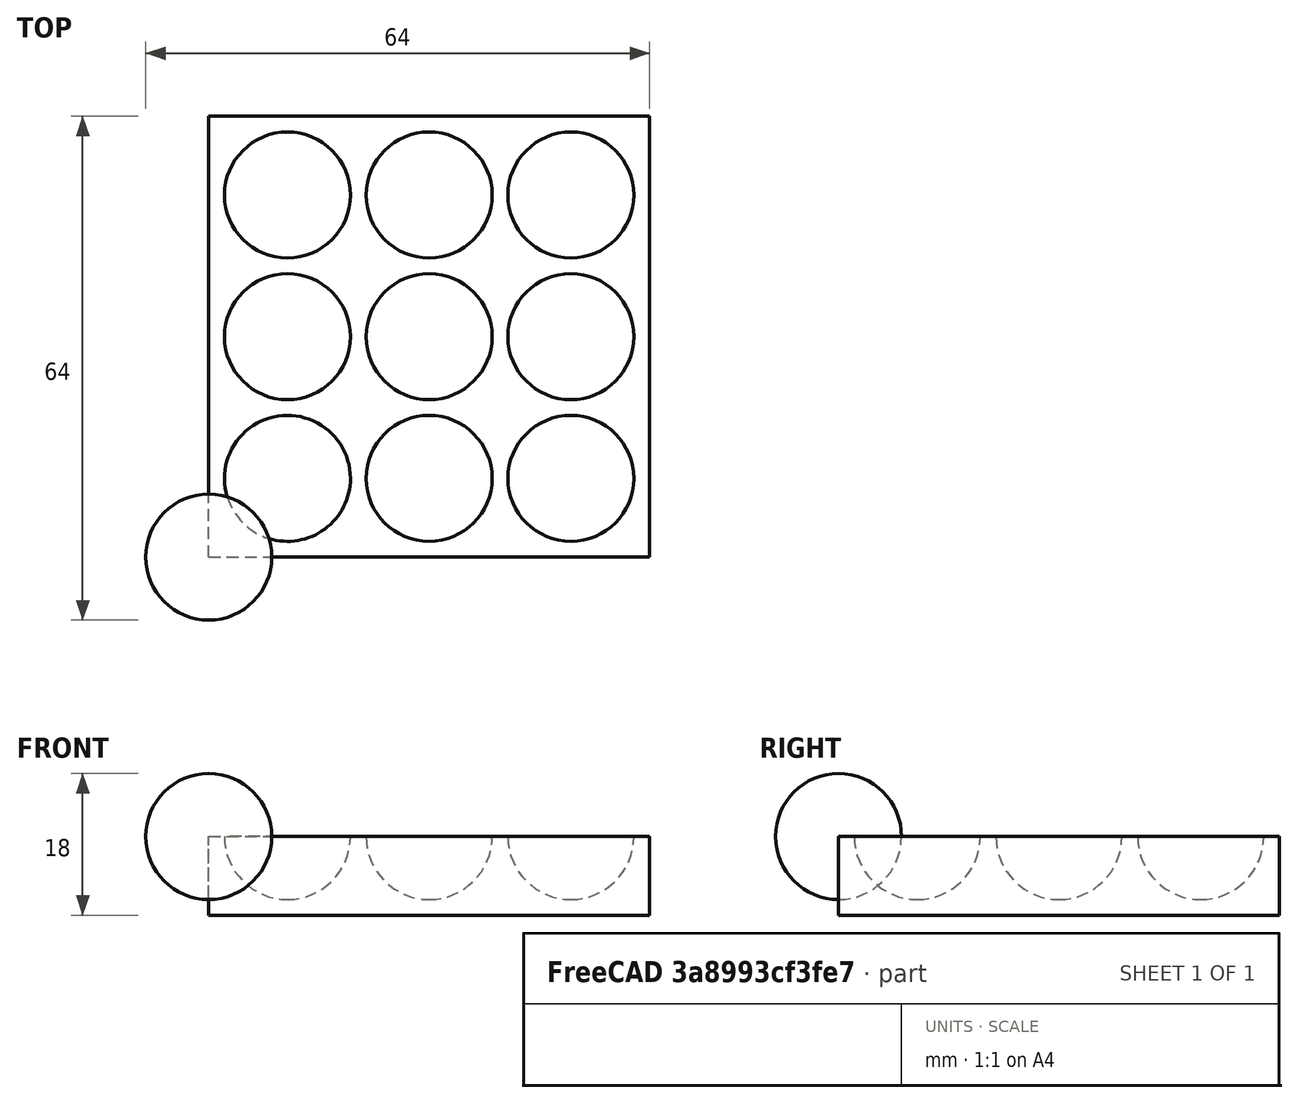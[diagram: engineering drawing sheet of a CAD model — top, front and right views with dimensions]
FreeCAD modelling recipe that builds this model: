
FCSTD DOCUMENT  (FreeCAD 0.21R33694 (Git))
Label: OJT1_T13P01_caniquero
License: All rights reserved
LicenseURL: http://en.wikipedia.org/wiki/All_rights_reserved
objects: Part::Sphere×1, Part::FeaturePython×1, Part::Box×1, Part::Cut×1
note: 3 computed .brp shape members not serialized (recipe doc carries the construction recipe); baked Part::Feature solids carry a one-line shape summary decoded from their .brp

FEATURE [Part::Sphere] Sphere
  Angle1 = -90
  Angle2 = 90
  Angle3 = 360
  AttacherType = Attacher::AttachEngine3D
  Radius = 8
FEATURE [Part::FeaturePython] Array  # Draft array (typed FeaturePython)
  AlwaysSyncPlacement = false
  Angle = 360
  ArrayType = 0
  Axis = (0,0,1)
  Base = -> Sphere
  Center = (0,0,0)
  Count = 9
  ExpandArray = false
  Fuse = false
  IntervalAxis = (0,0,0)
  IntervalX = (18,0,0)
  IntervalY = (0,18,0)
  IntervalZ = (0,0,100)
  NumberCircles = 3
  NumberPolar = 5
  NumberX = 3
  NumberY = 3
  NumberZ = 1
  Placement = pos=(10,10,0) rot=(0,0,1;0rad)
  PlacementList = 9 placements: [(0,0,0),(0,18,0),(0,36,0),(18,0,0),(18,18,0),(18,36,0),(36,0,0),(36,18,0),(36,36,0)]
  RadialDistance = 50
  ScaleList = (9) [(1,1,1),(1,1,1),(1,1,1),(1,1,1),(1,1,1),(1,1,1),(1,1,1),(1,1,1),(1,1,1)]
  Symmetry = 1
  TangentialDistance = 25
FEATURE [Part::Box] Box  label="Cube"
  AttacherType = Attacher::AttachEngine3D
  Height = 10
  Length = 56
  Placement = pos=(0,0,-10) rot=(0,0,1;0rad)
  Width = 56
FEATURE [Part::Cut] Cut
  Base = -> Box
  Refine = true
  Tool = -> Array
